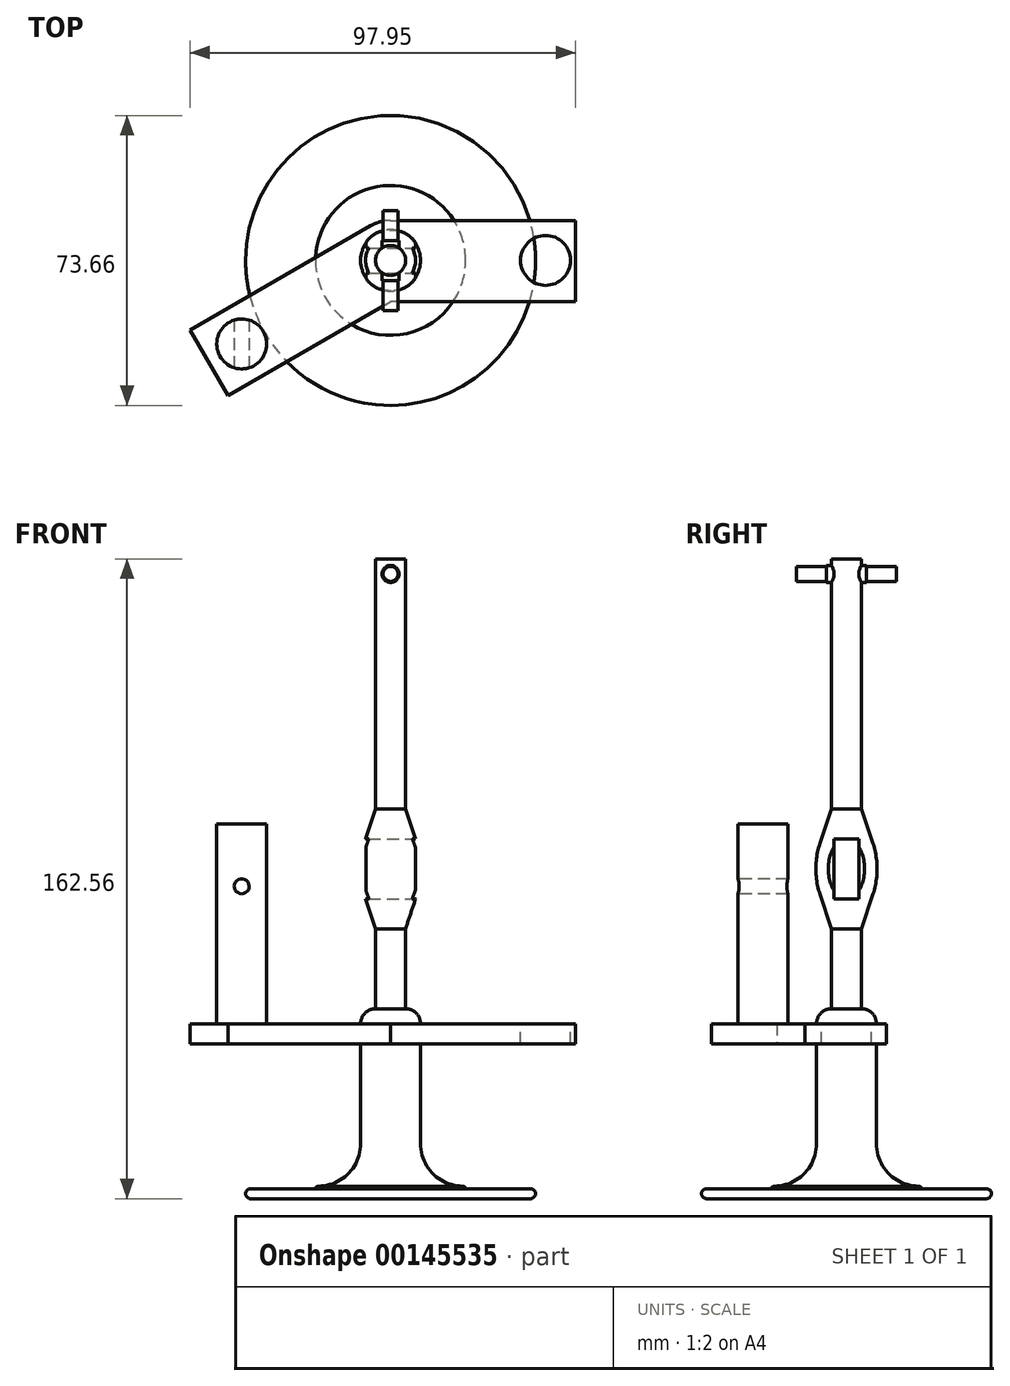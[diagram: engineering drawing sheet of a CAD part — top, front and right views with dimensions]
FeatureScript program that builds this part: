
annotation { "Feature Type Name" : "Feature", "Feature Type Description" : "" }
export const myFeature = defineFeature(function(context is Context, id is Id, definition is map)
    precondition{}
    {
        {
            var Q0;
            Q0=qCreatedBy(makeId("Front.planeOp"),FACE);
            var sketch = newSketch(context, id + "F0", { "sketchPlane" : qUnion([Q0])});
            skLineSegment(sketch, "E0", {"start": v(0, 0) * mm, "end": v(36.83, 0) * mm});
            skLineSegment(sketch, "E1", {"start": v(36.83, 0) * mm, "end": v(36.83, 2.54) * mm});
            skLineSegment(sketch, "E2", {"start": v(36.83, 2.54) * mm, "end": v(19.05, 2.54) * mm});
            skLineSegment(sketch, "E3", {"start": v(19.05, 2.54) * mm, "end": v(19.05, 3.18) * mm});
            skLineSegment(sketch, "E4", {"start": v(19.05, 3.18) * mm, "end": v(7.62, 3.17) * mm});
            skLineSegment(sketch, "E5", {"start": v(7.62, 3.17) * mm, "end": v(7.62, 48.26) * mm});
            skLineSegment(sketch, "E6", {"start": v(7.62, 48.26) * mm, "end": v(0, 48.26) * mm});
            skLineSegment(sketch, "E7", {"start": v(0, 48.26) * mm, "end": v(0, 0) * mm});
            skPoint(sketch, "E8.oppositeSnap0", {"position": v(3.8, 48.26) * mm});
            skLineSegment(sketch, "E8.bottom", {"start": v(0, 48.26) * mm, "end": v(3.8, 48.26) * mm});
            skLineSegment(sketch, "E8.top", {"start": v(0, 68.58) * mm, "end": v(3.8, 68.58) * mm});
            skLineSegment(sketch, "E8.left", {"start": v(0, 48.26) * mm, "end": v(0, 68.58) * mm});
            skLineSegment(sketch, "E8.right", {"start": v(3.81, 48.26) * mm, "end": v(3.81, 68.58) * mm});
            skLineSegment(sketch, "E9", {"start": v(3.8, 68.58) * mm, "end": v(8.89, 83.82) * mm});
            skLineSegment(sketch, "E10", {"start": v(0, 68.58) * mm, "end": v(0, 99.06) * mm});
            skLineSegment(sketch, "E11", {"start": v(0, 99.06) * mm, "end": v(3.8, 99.06) * mm});
            skLineSegment(sketch, "E12", {"start": v(3.8, 99.06) * mm, "end": v(8.89, 83.82) * mm});
            skLineSegment(sketch, "E13", {"start": v(0, 99.06) * mm, "end": v(0, 162.56) * mm});
            skLineSegment(sketch, "E14", {"start": v(0, 162.56) * mm, "end": v(3.8, 162.56) * mm});
            skLineSegment(sketch, "E15", {"start": v(3.8, 162.56) * mm, "end": v(3.8, 99.06) * mm});
            skSolve(sketch);
        }
        {
            var Q0;
            Q0 = qSketchRegion(id + "F0", true);
            var Q1;
            Q1=sQuery(id+"F0.wireOp",EDGE,"E7");
            revolve(context, id + "F1", {"entities" : qUnion([Q0]), "axis" : qUnion([Q1]), "revolveType" : RevolveType.FULL});
        }
        {
            var Q0;
            Q0=makeQuery(id+"F1.opRevolve","SWEPT_EDGE",EDGE,{"disambiguationData":[OSD([sQuery(id+"F0.wireOp",EDGE,"E1"),sQuery(id+"F0.wireOp",EDGE,"E2")])]});
            var Q1;
            Q1=makeQuery(id+"F1.opRevolve","SWEPT_EDGE",EDGE,{"disambiguationData":[OSD([sQuery(id+"F0.wireOp",EDGE,"E0"),sQuery(id+"F0.wireOp",EDGE,"E1")])]});
            fillet(context, id + "F2", {"entities" : qUnion([Q0, Q1]), "radius" : 1.27 * mm, "tangentPropagation" : true, "allowEdgeOverflow" : false});
        }
        {
            var Q0;
            Q0=makeQuery(id+"F1.opRevolve","SWEPT_EDGE",EDGE,{"disambiguationData":[OSD([sQuery(id+"F0.wireOp",EDGE,"E3"),sQuery(id+"F0.wireOp",EDGE,"E4")])]});
            fillet(context, id + "F3", {"entities" : qUnion([Q0]), "radius" : 0.64 * mm, "tangentPropagation" : true, "allowEdgeOverflow" : false});
        }
        {
            var Q0;
            Q0=makeQuery(id+"F1.opRevolve","SWEPT_EDGE",EDGE,{"disambiguationData":[OSD([sQuery(id+"F0.wireOp",EDGE,"E4"),sQuery(id+"F0.wireOp",EDGE,"E5")])]});
            fillet(context, id + "F4", {"entities" : qUnion([Q0]), "radius" : 10.8 * mm, "tangentPropagation" : true, "allowEdgeOverflow" : false});
        }
        {
            var Q0;
            Q0=makeQuery(id+"F1.opRevolve","SWEPT_EDGE",EDGE,{"disambiguationData":[OSD([sQuery(id+"F0.wireOp",EDGE,"E5"),sQuery(id+"F0.wireOp",EDGE,"E6")])]});
            fillet(context, id + "F5", {"entities" : qUnion([Q0]), "radius" : 3.8 * mm, "allowEdgeOverflow" : false});
        }
        {
            var Q0;
            Q0=qCreatedBy(makeId("Right.planeOp"),FACE);
            var sketch = newSketch(context, id + "F6", { "sketchPlane" : qUnion([Q0])});
            skLineSegment(sketch, "E16.bottom", {"start": v(-3.18, 91.44) * mm, "end": v(3.17, 91.44) * mm});
            skLineSegment(sketch, "E16.top", {"start": v(-3.18, 76.2) * mm, "end": v(3.17, 76.2) * mm});
            skLineSegment(sketch, "E16.left", {"start": v(-3.18, 91.44) * mm, "end": v(-3.18, 76.2) * mm});
            skLineSegment(sketch, "E16.right", {"start": v(3.17, 91.44) * mm, "end": v(3.17, 76.2) * mm});
            skSolve(sketch);
        }
        {
            var Q0;
            Q0 = qSketchRegion(id + "F6", true);
            extrude(context, id + "F7", {"entities" : qUnion([Q0]), "operationType" : NewBodyOperationType.REMOVE, "endBound" : BoundingType.SYMMETRIC, "oppositeDirection" : true, "depth" : 50.8 * mm});
        }
        {
            var Q0;
            Q0=qCreatedBy(makeId("Front.planeOp"),FACE);
            var sketch = newSketch(context, id + "F8", { "sketchPlane" : qUnion([Q0])});
            skLineSegment(sketch, "E17.bottom", {"start": v(-8.3, 91.44) * mm, "end": v(8.3, 91.44) * mm});
            skLineSegment(sketch, "E17.top", {"start": v(-8.3, 76.2) * mm, "end": v(8.3, 76.2) * mm});
            skLineSegment(sketch, "E17.left", {"start": v(-8.3, 91.44) * mm, "end": v(-8.3, 76.2) * mm});
            skLineSegment(sketch, "E17.right", {"start": v(8.3, 91.44) * mm, "end": v(8.3, 76.2) * mm});
            skLineSegment(sketch, "E18", {"start": v(-6.27, 91.44) * mm, "end": v(-6.27, 76.2) * mm});
            skLineSegment(sketch, "E19", {"start": v(6.27, 91.44) * mm, "end": v(6.27, 76.2) * mm});
            skSolve(sketch);
        }
        {
            var Q0;
            {var subQ0=sQuery(id+"F8.wireOp",EDGE,"E17.left");Q0=makeQuery(id+"F8.imprint","IMPRINT",FACE,{"disambiguationData":[TD([[makeQuery(id+"F8.imprint","IMPRINT",EDGE,{"derivedFrom":subQ0}),1.0]])]});}
            var Q1;
            {var subQ0=sQuery(id+"F8.wireOp",EDGE,"E17.right");Q1=makeQuery(id+"F8.imprint","IMPRINT",FACE,{"disambiguationData":[TD([[makeQuery(id+"F8.imprint","IMPRINT",EDGE,{"derivedFrom":subQ0}),-1.0]])]});}
            extrude(context, id + "F9", {"entities" : qUnion([Q0, Q1]), "operationType" : NewBodyOperationType.REMOVE, "endBound" : BoundingType.SYMMETRIC, "depth" : 76.2 * mm});
        }
        {
            var Q0;
            {var subQ0=sQuery(id+"F0.wireOp",EDGE,"E9");var subQ1=sQuery(id+"F0.wireOp",EDGE,"E12");Q0=makeQuery(id+"F7.boolean.opBoolean","SPLIT",EDGE,{"disambiguationData":[TD([makeQuery(id+"F7.opExtrude","SWEPT_FACE",FACE,{"disambiguationData":[OSD([sQuery(id+"F6.wireOp",EDGE,"E16.left")])]})])],"derivedFrom":makeQuery(id+"F1.opRevolve","SWEPT_EDGE",EDGE,{"disambiguationData":[OSD([subQ0,subQ1])]})});}
            var Q1;
            {var subQ0=sQuery(id+"F0.wireOp",EDGE,"E9");var subQ1=sQuery(id+"F0.wireOp",EDGE,"E12");Q1=makeQuery(id+"F7.boolean.opBoolean","SPLIT",EDGE,{"disambiguationData":[TD([makeQuery(id+"F7.opExtrude","SWEPT_FACE",FACE,{"disambiguationData":[OSD([sQuery(id+"F6.wireOp",EDGE,"E16.right")])]})])],"derivedFrom":makeQuery(id+"F1.opRevolve","SWEPT_EDGE",EDGE,{"disambiguationData":[OSD([subQ0,subQ1])]})});}
            fillet(context, id + "F10", {"entities" : qUnion([Q0, Q1]), "radius" : 20.32 * mm, "tangentPropagation" : true, "allowEdgeOverflow" : false});
        }
        {
            var Q0;
            Q0=qCreatedBy(makeId("Top.planeOp"),FACE);
            cPlane(context, id + "F11", {"entities" : qUnion([Q0]), "cplaneType" : CPlaneType.OFFSET, "offset" : 41.9 * mm, "width" : 152.4 * mm, "height" : 152.4 * mm});
        }
        {
            var Q0;
            Q0=qCreatedBy(id+"F11.planeOp",FACE);
            var sketch = newSketch(context, id + "F12", { "sketchPlane" : qUnion([Q0])});
            skCircle(sketch, "E20", {"center": v(0, 0) * mm, "radius": 10.16 * mm});
            skLineSegment(sketch, "E21", {"start": v(0, 10.16) * mm, "end": v(47, 10.16) * mm});
            skLineSegment(sketch, "E22", {"start": v(47, 10.16) * mm, "end": v(47, -10.5) * mm});
            skLineSegment(sketch, "E23", {"start": v(47, -10.5) * mm, "end": v(0, -10.5) * mm});
            skLineSegment(sketch, "E24", {"start": v(-41.34, -34.36) * mm, "end": v(0, -10.5) * mm});
            skCircle(sketch, "E25", {"center": v(0, 0) * mm, "radius": 7.62 * mm});
            skLineSegment(sketch, "E26", {"start": v(-5.08, 8.8) * mm, "end": v(-50.96, -17.7) * mm});
            skLineSegment(sketch, "E27", {"start": v(-41.34, -34.36) * mm, "end": v(-50.96, -17.7) * mm});
            skSolve(sketch);
        }
        {
            var Q0;
            {var subQ0=sQuery(id+"F12.wireOp",EDGE,"E21");Q0=makeQuery(id+"F12.imprint","IMPRINT",FACE,{"disambiguationData":[TD([[makeQuery(id+"F12.imprint","IMPRINT",EDGE,{"derivedFrom":subQ0}),-1.0]])]});}
            var Q1;
            Q1=makeQuery(id+"F12.imprint","IMPRINT",FACE,{"disambiguationData":[TD([[makeQuery(id+"F12.imprint","IMPRINT",EDGE,{"derivedFrom":sQuery(id+"F12.wireOp",EDGE,"fWG1eO3T-Lf6Q-2OwK-AFQs-8Faahlzc7EVk")}),1.0]])]});
            var Q2;
            Q2=makeQuery(id+"F12.imprint","IMPRINT",FACE,{"disambiguationData":[TD([[makeQuery(id+"F12.imprint","IMPRINT",EDGE,{"derivedFrom":sQuery(id+"F12.wireOp",EDGE,"E25")}),-1.0]])]});
            extrude(context, id + "F13", {"entities" : qUnion([Q0, Q1, Q2]), "operationType" : NewBodyOperationType.ADD, "endBound" : BoundingType.SYMMETRIC, "depth" : 5.08 * mm});
        }
        {
            var Q0;
            Q0=makeQuery(id+"F13.opExtrude","CAP_FACE",FACE,{"disambiguationData":[OSD([sQuery(id+"F12.wireOp",EDGE,"E20"),sQuery(id+"F12.wireOp",EDGE,"E21"),sQuery(id+"F12.wireOp",EDGE,"E22"),sQuery(id+"F12.wireOp",EDGE,"E23"),sQuery(id+"F12.wireOp",EDGE,"E24"),sQuery(id+"F12.wireOp",EDGE,"E25"),sQuery(id+"F12.wireOp",EDGE,"E26"),sQuery(id+"F12.wireOp",EDGE,"E27")])],"isStart":false});
            var sketch = newSketch(context, id + "F14", { "sketchPlane" : qUnion([Q0])});
            skCircle(sketch, "E28", {"center": v(-37.81, -21.22) * mm, "radius": 6.35 * mm});
            skPoint(sketch, "E29", {"position": v(-37.73, -14.87) * mm});
            skCircle(sketch, "E30", {"center": v(39.37, 0) * mm, "radius": 6.35 * mm});
            skSolve(sketch);
        }
        {
            var Q0;
            Q0=makeQuery(id+"F14.imprint","IMPRINT",FACE,{"disambiguationData":[TD([[makeQuery(id+"F14.imprint","IMPRINT",EDGE,{"derivedFrom":sQuery(id+"F14.wireOp",EDGE,"E28")}),1.0]])]});
            extrude(context, id + "F15", {"entities" : qUnion([Q0]), "operationType" : NewBodyOperationType.ADD, "depth" : 50.8 * mm});
        }
        {
            var Q0;
            Q0=qCreatedBy(makeId("Front.planeOp"),FACE);
            var Q1;
            Q1=sQuery(id+"F14.wireOp",VERTEX,"E28.center");
            cPlane(context, id + "F16", {"entities" : qUnion([Q0, Q1]), "cplaneType" : CPlaneType.PLANE_POINT, "offset" : 25.4 * mm, "width" : 152.4 * mm, "height" : 152.4 * mm});
        }
        {
            var Q0;
            Q0=qCreatedBy(id+"F16.planeOp",FACE);
            var sketch = newSketch(context, id + "F17", { "sketchPlane" : qUnion([Q0])});
            skCircle(sketch, "E31", {"center": v(-37.81, 79.38) * mm, "radius": 1.9 * mm});
            skSolve(sketch);
        }
        {
            var Q0;
            Q0 = qSketchRegion(id + "F17", true);
            extrude(context, id + "F18", {"entities" : qUnion([Q0]), "operationType" : NewBodyOperationType.REMOVE, "endBound" : BoundingType.SYMMETRIC, "oppositeDirection" : true, "depth" : 25.4 * mm});
        }
        {
            var Q0;
            Q0=makeQuery(id+"F14.imprint","IMPRINT",FACE,{"disambiguationData":[TD([[makeQuery(id+"F14.imprint","IMPRINT",EDGE,{"derivedFrom":sQuery(id+"F14.wireOp",EDGE,"E30")}),1.0]])]});
            var Q1;
            Q1=makeQuery(id+"F13.opExtrude","CAP_FACE",FACE,{"disambiguationData":[OSD([sQuery(id+"F12.wireOp",EDGE,"E20"),sQuery(id+"F12.wireOp",EDGE,"E21"),sQuery(id+"F12.wireOp",EDGE,"E22"),sQuery(id+"F12.wireOp",EDGE,"E23"),sQuery(id+"F12.wireOp",EDGE,"E24"),sQuery(id+"F12.wireOp",EDGE,"E25"),sQuery(id+"F12.wireOp",EDGE,"E26"),sQuery(id+"F12.wireOp",EDGE,"E27")])],"isStart":true});
            extrude(context, id + "F19", {"entities" : qUnion([Q0]), "operationType" : NewBodyOperationType.REMOVE, "endBound" : BoundingType.UP_TO_SURFACE, "oppositeDirection" : true, "endBoundEntityFace" : qUnion([Q1]), "depth" : 25.4 * mm});
        }
        {
            var Q0;
            Q0=qCreatedBy(makeId("Front.planeOp"),FACE);
            var sketch = newSketch(context, id + "F20", { "sketchPlane" : qUnion([Q0])});
            skCircle(sketch, "E32", {"center": v(0, 158.75) * mm, "radius": 2.16 * mm});
            skSolve(sketch);
        }
        {
            var Q0;
            Q0 = qSketchRegion(id + "F20", true);
            extrude(context, id + "F21", {"entities" : qUnion([Q0]), "operationType" : NewBodyOperationType.ADD, "endBound" : BoundingType.SYMMETRIC, "depth" : 10.16 * mm});
        }
        {
            var Q0;
            Q0=makeQuery(id+"F21.opExtrude","CAP_FACE",FACE,{"disambiguationData":[OSD([sQuery(id+"F20.wireOp",EDGE,"E32")])],"isStart":false});
            var sketch = newSketch(context, id + "F22", { "sketchPlane" : qUnion([Q0])});
            skCircle(sketch, "E33", {"center": v(0, 158.75) * mm, "radius": 1.9 * mm});
            skSolve(sketch);
        }
        {
            var Q0;
            Q0 = qSketchRegion(id + "F22", true);
            extrude(context, id + "F23", {"entities" : qUnion([Q0]), "operationType" : NewBodyOperationType.ADD, "depth" : 7.62 * mm});
        }
        {
            var Q0;
            Q0=makeQuery(id+"F21.opExtrude","CAP_FACE",FACE,{"disambiguationData":[OSD([sQuery(id+"F20.wireOp",EDGE,"E32")])],"isStart":true});
            var sketch = newSketch(context, id + "F24", { "sketchPlane" : qUnion([Q0])});
            skCircle(sketch, "E34", {"center": v(0, 158.75) * mm, "radius": 1.9 * mm});
            skSolve(sketch);
        }
        {
            var Q0;
            Q0 = qSketchRegion(id + "F24", true);
            extrude(context, id + "F25", {"entities" : qUnion([Q0]), "operationType" : NewBodyOperationType.ADD, "depth" : 7.62 * mm});
        }
    });
